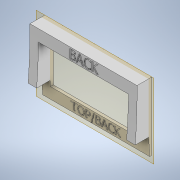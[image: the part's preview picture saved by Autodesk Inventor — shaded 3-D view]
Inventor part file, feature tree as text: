
AUTODESK INVENTOR PART (.ipt)
format: ipt  version: 2021.1 (Build 251245000, 245)  size: 593,408 bytes
history: native  units: in
note: dims shown in document units (in); Inventor stores cm internally (conversion verified against a paired STEP export)
features: sketch x3, extrude x2, emboss x2, plane x1
ambient origin geometry x8: Origin, YZ Plane, XZ Plane, XY Plane, X Axis, Y Axis, Z Axis, Center Point
bodies: Solid1 (feature_tree)
feature tree (8):
  extrude  "Extrusion1"  Depth=4.0in
  extrude  "Extrusion2"  Depth=0.0835in
  plane  "Work Plane1"
  emboss  "Emboss1"
  emboss  "Emboss2"
  sketch  "Sketch2"  dims[d0=0.6in d1=4.0in]
  sketch  "Sketch3"  dims[d3=2.0in d4=0.0835in]
  sketch  "Sketch4"  dims[d5=24.0in d6=4.0in d7=24.0in d8=0.75in d9=1.525in d10=0.1in d11=3.05in d12=4.82in d13=0.0in d14=4.05in d15=2.0in d16=0.0in d17=0.0in d18=0.2625in d19=0.04in d20=0.0in d21=0.2625in d22=0.04in d23=0.0in d24=0.525in]
